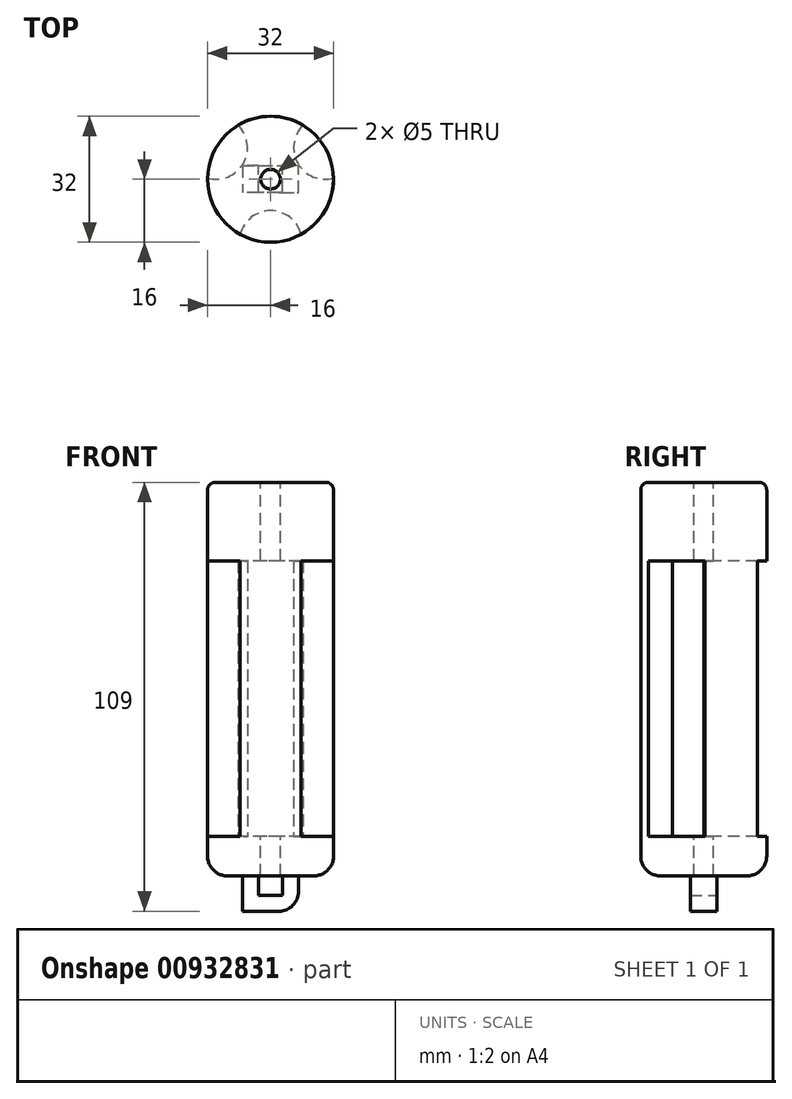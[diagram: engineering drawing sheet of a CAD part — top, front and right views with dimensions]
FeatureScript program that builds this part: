
annotation { "Feature Type Name" : "Feature", "Feature Type Description" : "" }
export const myFeature = defineFeature(function(context is Context, id is Id, definition is map)
    precondition{}
    {
        {
            var Q0;
            Q0=qCreatedBy(makeId("Top.planeOp"),FACE);
            var sketch = newSketch(context, id + "F0", { "sketchPlane" : qUnion([Q0])});
            skCircle(sketch, "E0", {"center": v(0, 0) * mm, "radius": 16 * mm});
            skCircle(sketch, "E1.cCircle", {"center": v(0, 0) * mm, "radius": 16 * mm, "construction": true});
            skArc(sketch, "E2", {"start": v(-16, 0.3) * mm, "mid": v(-6.93, 4) * mm, "end": v(-8.25, 13.7) * mm});
            skArc(sketch, "E3", {"start": v(8.25, 13.7) * mm, "mid": v(6.93, 4) * mm, "end": v(16, 0.3) * mm});
            skArc(sketch, "E4", {"start": v(7.75, -14) * mm, "mid": v(0, -8) * mm, "end": v(-7.75, -14) * mm});
            skPoint(sketch, "E4.centerSnap0", {"position": v(0, -8) * mm});
            skSolve(sketch);
        }
        {
            var Q0;
            {var subQ3=sQuery(id+"F0.wireOp",EDGE,"E2");Q0=makeQuery(id+"F0.imprint","IMPRINT",FACE,{"disambiguationData":[TD([[makeQuery(id+"F0.imprint","IMPRINT",EDGE,{"derivedFrom":subQ3}),-1.0]])]});}
            var Q1;
            {var subQ0=sQuery(id+"F0.wireOp",EDGE,"E2");Q1=makeQuery(id+"F0.imprint","IMPRINT",FACE,{"disambiguationData":[TD([[makeQuery(id+"F0.imprint","IMPRINT",EDGE,{"derivedFrom":subQ0}),1.0]])]});}
            var Q2;
            {var subQ0=sQuery(id+"F0.wireOp",EDGE,"E3");Q2=makeQuery(id+"F0.imprint","IMPRINT",FACE,{"disambiguationData":[TD([[makeQuery(id+"F0.imprint","IMPRINT",EDGE,{"derivedFrom":subQ0}),1.0]])]});}
            var Q3;
            {var subQ0=sQuery(id+"F0.wireOp",EDGE,"E4");Q3=makeQuery(id+"F0.imprint","IMPRINT",FACE,{"disambiguationData":[TD([[makeQuery(id+"F0.imprint","IMPRINT",EDGE,{"derivedFrom":subQ0}),1.0]])]});}
            extrude(context, id + "F1", {"entities" : qUnion([Q0, Q1, Q2, Q3]), "depth" : -10 * mm, "offsetDistance" : 25 * mm});
        }
        {
            var Q0;
            {var subQ0=sQuery(id+"F0.wireOp",EDGE,"E2");Q0=makeQuery(id+"F0.imprint","IMPRINT",FACE,{"disambiguationData":[TD([[makeQuery(id+"F0.imprint","IMPRINT",EDGE,{"derivedFrom":subQ0}),1.0]])]});}
            var Q1;
            {var subQ0=sQuery(id+"F0.wireOp",EDGE,"E3");Q1=makeQuery(id+"F0.imprint","IMPRINT",FACE,{"disambiguationData":[TD([[makeQuery(id+"F0.imprint","IMPRINT",EDGE,{"derivedFrom":subQ0}),1.0]])]});}
            var Q2;
            {var subQ0=sQuery(id+"F0.wireOp",EDGE,"E4");Q2=makeQuery(id+"F0.imprint","IMPRINT",FACE,{"disambiguationData":[TD([[makeQuery(id+"F0.imprint","IMPRINT",EDGE,{"derivedFrom":subQ0}),1.0]])]});}
            extrude(context, id + "F2", {"entities" : qUnion([Q0, Q1, Q2]), "operationType" : NewBodyOperationType.ADD, "depth" : 70 * mm, "offsetDistance" : 25 * mm});
        }
        {
            var Q0;
            Q0=makeQuery(id+"F2.opExtrude","CAP_FACE",FACE,{"disambiguationData":[OSD([sQuery(id+"F0.wireOp",EDGE,"E0"),sQuery(id+"F0.wireOp",EDGE,"E4")])],"isStart":false});
            var sketch = newSketch(context, id + "F3", { "sketchPlane" : qUnion([Q0])});
            skArc(sketch, "E5.0.0", {"start": v(-7.75, -14) * mm, "mid": v(0, -8) * mm, "end": v(7.75, -14) * mm});
            skArc(sketch, "E5.0.1", {"start": v(7.75, -14) * mm, "mid": v(13.86, -8) * mm, "end": v(16, 0.3) * mm});
            skArc(sketch, "E5.0.2", {"start": v(16, 0.3) * mm, "mid": v(6.93, 4) * mm, "end": v(8.25, 13.7) * mm});
            skArc(sketch, "E5.0.3", {"start": v(8.25, 13.7) * mm, "mid": v(0, 16) * mm, "end": v(-8.25, 13.7) * mm});
            skArc(sketch, "E5.0.4", {"start": v(-8.25, 13.7) * mm, "mid": v(-6.93, 4) * mm, "end": v(-16, 0.3) * mm});
            skArc(sketch, "E5.0.5", {"start": v(-16, 0.3) * mm, "mid": v(-13.86, -8) * mm, "end": v(-7.75, -14) * mm});
            skSolve(sketch);
        }
        {
            var Q0;
            Q0=makeQuery(id+"F3.imprint","IMPRINT",FACE,{"disambiguationData":[TD([[makeQuery(id+"F3.imprint","IMPRINT",EDGE,{"derivedFrom":sQuery(id+"F3.wireOp",EDGE,"E5.0.0")}),-1.0]])]});
            var Q1;
            Q1=makeQuery(id+"F2.opExtrude","CAP_FACE",FACE,{"disambiguationData":[OSD([sQuery(id+"F0.wireOp",EDGE,"E0"),sQuery(id+"F0.wireOp",EDGE,"E2")])],"isStart":false});
            var Q2;
            Q2=makeQuery(id+"F2.opExtrude","CAP_FACE",FACE,{"disambiguationData":[OSD([sQuery(id+"F0.wireOp",EDGE,"E0"),sQuery(id+"F0.wireOp",EDGE,"E3")])],"isStart":false});
            var Q3;
            Q3=makeQuery(id+"F3.imprint","IMPRINT",FACE,{"disambiguationData":[TD([[makeQuery(id+"F3.imprint","IMPRINT",EDGE,{"derivedFrom":sQuery(id+"F3.wireOp",EDGE,"E5.0.0")}),1.0]])]});
            extrude(context, id + "F4", {"entities" : qUnion([Q0, Q1, Q2, Q3]), "operationType" : NewBodyOperationType.ADD, "depth" : 20 * mm, "offsetDistance" : 25 * mm});
        }
        {
            var Q0;
            {var subQ0=sQuery(id+"F0.wireOp",EDGE,"E0");Q0=makeQuery(id+"F4.boolean.opBoolean","MERGE",FACE,{"derivedFrom":[makeQuery(id+"F4.opExtrude","CAP_FACE",FACE,{"disambiguationData":[OSD([subQ0,sQuery(id+"F0.wireOp",EDGE,"E3")])],"isStart":false}),makeQuery(id+"F4.opExtrude","CAP_FACE",FACE,{"disambiguationData":[OSD([subQ0,sQuery(id+"F0.wireOp",EDGE,"E2")])],"isStart":false}),makeQuery(id+"F4.opExtrude","CAP_FACE",FACE,{"disambiguationData":[OSD([subQ0,sQuery(id+"F3.wireOp",EDGE,"E5.0.1"),sQuery(id+"F3.wireOp",EDGE,"E5.0.2"),sQuery(id+"F3.wireOp",EDGE,"E5.0.3"),sQuery(id+"F3.wireOp",EDGE,"E5.0.4"),sQuery(id+"F3.wireOp",EDGE,"E5.0.5")])],"isStart":false})]});}
            var sketch = newSketch(context, id + "F5", { "sketchPlane" : qUnion([Q0])});
            skPoint(sketch, "E6", {"position": v(0, 0) * mm});
            skSolve(sketch);
        }
        {
            var Q0;
            Q0=sQuery(id+"F5.wireOp",VERTEX,"E6");
            var Q1;
            Q1=makeQuery(id+"F1.opExtrude","SWEPT_BODY",BODY,{"disambiguationData":[OSD([sQuery(id+"F0.wireOp",EDGE,"E0")])]});
            hole(context, id + "F6", {"style" : HoleStyle.SIMPLE, "endStyle" : HoleEndStyle.THROUGH, "holeDiameter" : 5 * mm, "majorDiameter" : 5 * mm, "isTappedThrough" : true, "tappedDepth" : 12 * mm, "tapClearance" : 3, "locations" : qUnion([Q0]), "scope" : qUnion([Q1])});
        }
        {
            var Q0;
            Q0=makeQuery(id+"F1.opExtrude","CAP_FACE",FACE,{"disambiguationData":[OSD([sQuery(id+"F0.wireOp",EDGE,"E0")])],"isStart":false});
            var sketch = newSketch(context, id + "F7", { "sketchPlane" : qUnion([Q0])});
            skLineSegment(sketch, "E7.top", {"start": v(0, 3.4) * mm, "end": v(7.09, 3.4) * mm});
            skLineSegment(sketch, "E7.right", {"start": v(7.09, 0) * mm, "end": v(7.09, 3.4) * mm});
            skLineSegment(sketch, "E8.MirrorCS", {"start": v(7.09, 0) * mm, "end": v(7.09, -3.4) * mm});
            skLineSegment(sketch, "E9.MirrorCS", {"start": v(-7.09, 0) * mm, "end": v(-7.09, 3.4) * mm});
            skLineSegment(sketch, "E10.MirrorCS", {"start": v(-7.09, 0) * mm, "end": v(-7.09, -3.4) * mm});
            skLineSegment(sketch, "E11.MirrorCS", {"start": v(0, -3.4) * mm, "end": v(-7.09, -3.4) * mm});
            skLineSegment(sketch, "E12.MirrorCS", {"start": v(0, 3.4) * mm, "end": v(-7.09, 3.4) * mm});
            skLineSegment(sketch, "E13", {"start": v(0, -3.4) * mm, "end": v(7.09, -3.4) * mm});
            skLineSegment(sketch, "E14.bottom", {"start": v(-3, 3.4) * mm, "end": v(3, 3.4) * mm});
            skLineSegment(sketch, "E14.top", {"start": v(-3, -3.4) * mm, "end": v(3, -3.4) * mm});
            skLineSegment(sketch, "E14.left", {"start": v(-3, 3.4) * mm, "end": v(-3, -3.4) * mm});
            skLineSegment(sketch, "E14.right", {"start": v(3, 3.4) * mm, "end": v(3, -3.4) * mm});
            skPoint(sketch, "E7.left.start.orphan", {"position": v(0, 0) * mm});
            skSolve(sketch);
        }
        {
            var Q0;
            Q0=makeQuery(id+"F7.imprint","IMPRINT",FACE,{"disambiguationData":[TD([[makeQuery(id+"F7.imprint","IMPRINT",EDGE,{"derivedFrom":sQuery(id+"F7.wireOp",EDGE,"E9.MirrorCS")}),-1.0]])]});
            var Q1;
            Q1=makeQuery(id+"F7.imprint","IMPRINT",FACE,{"disambiguationData":[TD([[makeQuery(id+"F7.imprint","IMPRINT",EDGE,{"derivedFrom":sQuery(id+"F7.wireOp",EDGE,"E7.top")}),-1.0]])]});
            extrude(context, id + "F8", {"entities" : qUnion([Q0, Q1]), "operationType" : NewBodyOperationType.ADD, "depth" : 5 * mm, "offsetDistance" : 25 * mm});
        }
        {
            var Q0;
            Q0=makeQuery(id+"F8.opExtrude","CAP_FACE",FACE,{"disambiguationData":[OSD([sQuery(id+"F7.wireOp",EDGE,"E7.top"),sQuery(id+"F7.wireOp",EDGE,"E7.right"),sQuery(id+"F7.wireOp",EDGE,"E8.MirrorCS"),sQuery(id+"F7.wireOp",EDGE,"E13"),sQuery(id+"F7.wireOp",EDGE,"E14.right")])],"isStart":false});
            var sketch = newSketch(context, id + "F9", { "sketchPlane" : qUnion([Q0])});
            skLineSegment(sketch, "E15.0.0", {"start": v(-7.09, 3.4) * mm, "end": v(-7.09, -3.4) * mm});
            skLineSegment(sketch, "E15.0.1", {"start": v(-7.09, -3.4) * mm, "end": v(-3, -3.4) * mm});
            skLineSegment(sketch, "E15.0.2", {"start": v(-3, -3.4) * mm, "end": v(-3, 3.4) * mm});
            skLineSegment(sketch, "E15.0.3", {"start": v(-3, 3.4) * mm, "end": v(-7.09, 3.4) * mm});
            skLineSegment(sketch, "E16.bottom", {"start": v(7.09, -3.4) * mm, "end": v(-7.09, -3.4) * mm});
            skLineSegment(sketch, "E16.top", {"start": v(7.09, 3.4) * mm, "end": v(-7.09, 3.4) * mm});
            skLineSegment(sketch, "E16.left", {"start": v(7.09, -3.4) * mm, "end": v(7.09, 3.4) * mm});
            skLineSegment(sketch, "E16.right", {"start": v(-7.09, -3.4) * mm, "end": v(-7.09, 3.4) * mm});
            skSolve(sketch);
        }
        {
            var Q0;
            Q0 = qSketchRegion(id + "F9", true);
            extrude(context, id + "F10", {"entities" : qUnion([Q0]), "operationType" : NewBodyOperationType.ADD, "depth" : 4 * mm, "offsetDistance" : 25 * mm});
        }
        {
            var Q0;
            Q0=makeQuery(id+"F10.opExtrude","CAP_EDGE",EDGE,{"disambiguationData":[OSD([sQuery(id+"F9.wireOp",EDGE,"E16.right")])],"isStart":false});
            var Q1;
            Q1=makeQuery(id+"F10.opExtrude","CAP_EDGE",EDGE,{"disambiguationData":[OSD([sQuery(id+"F9.wireOp",EDGE,"E16.left")])],"isStart":false});
            fillet(context, id + "F11", {"entities" : qUnion([Q0, Q1]), "radius" : 5 * mm, "tangentPropagation" : true, "allowEdgeOverflow" : false});
        }
        {
            var Q0;
            {var subQ0=sQuery(id+"F0.wireOp",EDGE,"E0");var subQ1=sQuery(id+"F0.wireOp",EDGE,"E2");var subQ2=sQuery(id+"F0.wireOp",EDGE,"E3");Q0=makeQuery(id+"F4.boolean.opBoolean","MERGE",EDGE,{"derivedFrom":[makeQuery(id+"F4.opExtrude","CAP_EDGE",EDGE,{"disambiguationData":[OSD([subQ0]),TDD([makeQuery(id+"F2.opExtrude","CAP_EDGE",EDGE,{"disambiguationData":[OSD([subQ0]),TDD([makeQuery(id+"F0.imprint","IMPRINT",EDGE,{"disambiguationData":[TD([[makeQuery(id+"F0.imprint","INTERSECT",VERTEX,{"disambiguationData":[OD(0.0)],"derivedFrom":[subQ0,subQ2]}),1.0]])],"derivedFrom":subQ0})])],"isStart":false})])],"isStart":false}),makeQuery(id+"F4.opExtrude","CAP_EDGE",EDGE,{"disambiguationData":[OSD([subQ0]),TDD([makeQuery(id+"F2.opExtrude","CAP_EDGE",EDGE,{"disambiguationData":[OSD([subQ0]),TDD([makeQuery(id+"F0.imprint","IMPRINT",EDGE,{"disambiguationData":[TD([[makeQuery(id+"F0.imprint","INTERSECT",VERTEX,{"disambiguationData":[OD(0.0)],"derivedFrom":[subQ0,subQ1]}),1.0]])],"derivedFrom":subQ0})])],"isStart":false})])],"isStart":false}),makeQuery(id+"F4.opExtrude","CAP_EDGE",EDGE,{"disambiguationData":[OSD([subQ0,sQuery(id+"F3.wireOp",EDGE,"E5.0.1"),sQuery(id+"F3.wireOp",EDGE,"E5.0.5")])],"isStart":false}),makeQuery(id+"F4.opExtrude","CAP_EDGE",EDGE,{"disambiguationData":[OSD([sQuery(id+"F3.wireOp",EDGE,"E5.0.3")])],"isStart":false})]});}
            fillet(context, id + "F12", {"entities" : qUnion([Q0]), "radius" : 2 * mm, "tangentPropagation" : true, "allowEdgeOverflow" : false});
        }
        {
            var Q0;
            Q0=makeQuery(id+"F1.opExtrude","CAP_EDGE",EDGE,{"disambiguationData":[OSD([sQuery(id+"F0.wireOp",EDGE,"E0")])],"isStart":false});
            fillet(context, id + "F13", {"entities" : qUnion([Q0]), "radius" : 5 * mm, "tangentPropagation" : true, "allowEdgeOverflow" : false});
        }
    });
